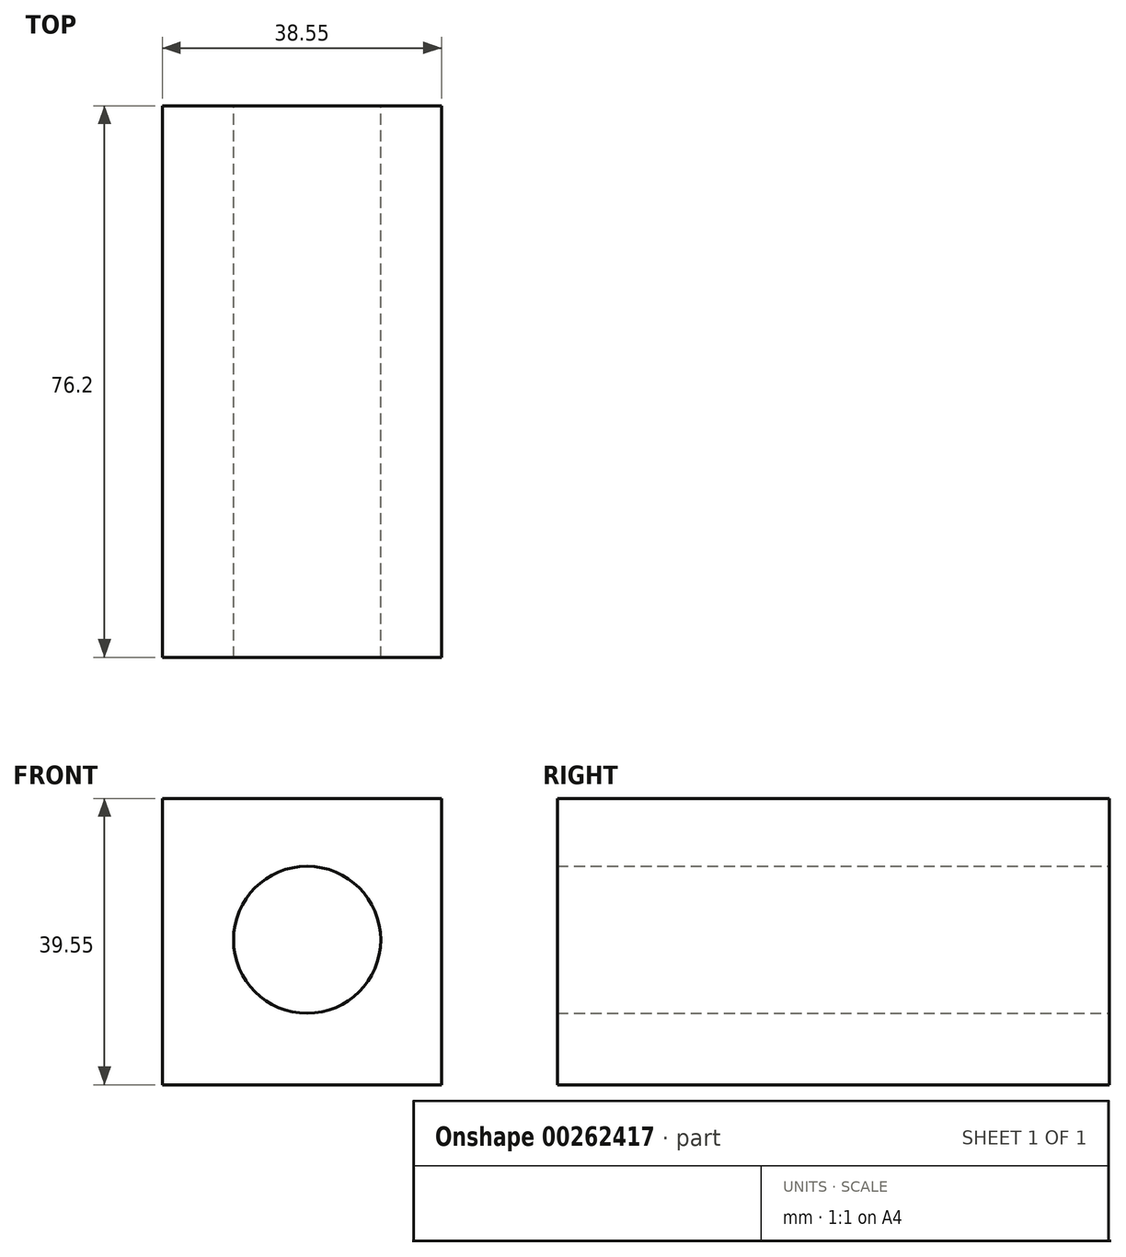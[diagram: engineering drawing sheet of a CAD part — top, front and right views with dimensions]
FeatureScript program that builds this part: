
annotation { "Feature Type Name" : "Feature", "Feature Type Description" : "" }
export const myFeature = defineFeature(function(context is Context, id is Id, definition is map)
    precondition{}
    {
        {
            var Q0;
            Q0=qCreatedBy(makeId("Front.planeOp"),FACE);
            var sketch = newSketch(context, id + "F0", { "sketchPlane" : qUnion([Q0])});
            skLineSegment(sketch, "E0.bottom", {"start": v(-24.73, 0) * mm, "end": v(-63.28, 0) * mm});
            skLineSegment(sketch, "E0.top", {"start": v(-24.73, 39.55) * mm, "end": v(-63.28, 39.55) * mm});
            skLineSegment(sketch, "E0.left", {"start": v(-24.73, 0) * mm, "end": v(-24.73, 39.55) * mm});
            skLineSegment(sketch, "E0.right", {"start": v(-63.28, 0) * mm, "end": v(-63.28, 39.55) * mm});
            skPoint(sketch, "E0.middle", {"position": v(-44, 19.78) * mm});
            skSolve(sketch);
        }
        {
            var Q0;
            Q0=makeQuery(id+"F0.imprint","IMPRINT",FACE,{"disambiguationData":[TD([[makeQuery(id+"F0.imprint","IMPRINT",EDGE,{"derivedFrom":sQuery(id+"F0.wireOp",EDGE,"E0.bottom")}),-1.0]])]});
            extrude(context, id + "F1", {"entities" : qUnion([Q0]), "depth" : 76.2 * mm});
        }
        {
            var Q0;
            Q0=makeQuery(id+"F1.opExtrude","CAP_FACE",FACE,{"disambiguationData":[OSD([sQuery(id+"F0.wireOp",EDGE,"E0.bottom"),sQuery(id+"F0.wireOp",EDGE,"E0.top"),sQuery(id+"F0.wireOp",EDGE,"E0.left"),sQuery(id+"F0.wireOp",EDGE,"E0.right")])],"isStart":false});
            var sketch = newSketch(context, id + "F2", { "sketchPlane" : qUnion([Q0])});
            skPoint(sketch, "E1", {"position": v(-44, 39.55) * mm});
            skPoint(sketch, "E2", {"position": v(-63.28, 19.78) * mm});
            skPoint(sketch, "E3", {"position": v(-44, 0) * mm});
            skPoint(sketch, "E4", {"position": v(-24.73, 19.78) * mm});
            skSolve(sketch);
        }
        {
            var Q0;
            Q0=makeQuery(id+"F1.opExtrude","CAP_FACE",FACE,{"disambiguationData":[OSD([sQuery(id+"F0.wireOp",EDGE,"E0.bottom"),sQuery(id+"F0.wireOp",EDGE,"E0.top"),sQuery(id+"F0.wireOp",EDGE,"E0.left"),sQuery(id+"F0.wireOp",EDGE,"E0.right")])],"isStart":true});
            var sketch = newSketch(context, id + "F3", { "sketchPlane" : qUnion([Q0])});
            skPoint(sketch, "E5", {"position": v(34.3, 29.68) * mm});
            skPoint(sketch, "E6", {"position": v(50.56, 29.28) * mm});
            skPoint(sketch, "E7", {"position": v(50.56, 13.34) * mm});
            skPoint(sketch, "E8", {"position": v(36.76, 13.34) * mm});
            skSolve(sketch);
        }
        {
            var Q0;
            Q0=makeQuery(id+"F3.imprint","IMPRINT",FACE,{"disambiguationData":[TD([[makeQuery(id+"F3.imprint","IMPRINT",EDGE,{"derivedFrom":makeQuery(id+"F1.opExtrude","CAP_EDGE",EDGE,{"disambiguationData":[OSD([sQuery(id+"F0.wireOp",EDGE,"E0.bottom")])],"isStart":true})}),1.0]])]});
            var sketch = newSketch(context, id + "F4", { "sketchPlane" : qUnion([Q0])});
            skPoint(sketch, "E9", {"position": v(43.28, 20.02) * mm});
            skSolve(sketch);
        }
        {
            var Q0;
            Q0=sQuery(id+"F4.wireOp",VERTEX,"E9");
            var Q1;
            Q1=makeQuery(id+"F1.opExtrude","SWEPT_BODY",BODY,{"disambiguationData":[OSD([sQuery(id+"F0.wireOp",EDGE,"E0.bottom"),sQuery(id+"F0.wireOp",EDGE,"E0.top"),sQuery(id+"F0.wireOp",EDGE,"E0.left"),sQuery(id+"F0.wireOp",EDGE,"E0.right")])]});
            hole(context, id + "F5", {"style" : HoleStyle.SIMPLE, "endStyle" : HoleEndStyle.THROUGH, "holeDiameter" : 20.32 * mm, "tappedDepth" : 12.7 * mm, "tapClearance" : 3, "startFromSketch" : true, "locations" : qUnion([Q0]), "scope" : qUnion([Q1])});
        }
    });
